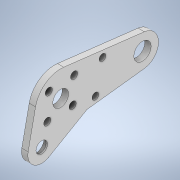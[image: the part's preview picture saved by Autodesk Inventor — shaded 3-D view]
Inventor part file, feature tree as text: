
AUTODESK INVENTOR PART (.ipt)
format: ipt  version: 2020 (Build 240168000, 168)  size: 428,032 bytes
history: native  units: mm
features: extrude x7, sketch x4, projected_geometry x3
ambient origin geometry x8: Origin, YZ Plane, XZ Plane, XY Plane, X Axis, Y Axis, Z Axis, Center Point
bodies: Body1 (feature_tree)
feature tree (14):
  extrude  "Выдавливание4"  Depth=18.6mm
  extrude  "Выдавливание5"  Depth=12.2mm
  extrude  "Выдавливание6"  Depth=9.7mm
  extrude  "Выдавливание7"  Depth=7.1mm
  sketch  "Эскиз7"
  extrude  "Выдавливание8"  Depth=38.82013mm
  extrude  "Выдавливание9"  Depth=38.8mm
  extrude  "Выдавливание10"  Depth=38.8mm
  sketch  "Эскиз4"
  projected_geometry  "Спроецированная петля3"
  sketch  "Эскиз5"
  sketch  "Эскиз6"
  projected_geometry  "Спроецированная петля4"
  projected_geometry  "Спроецированная петля5"
